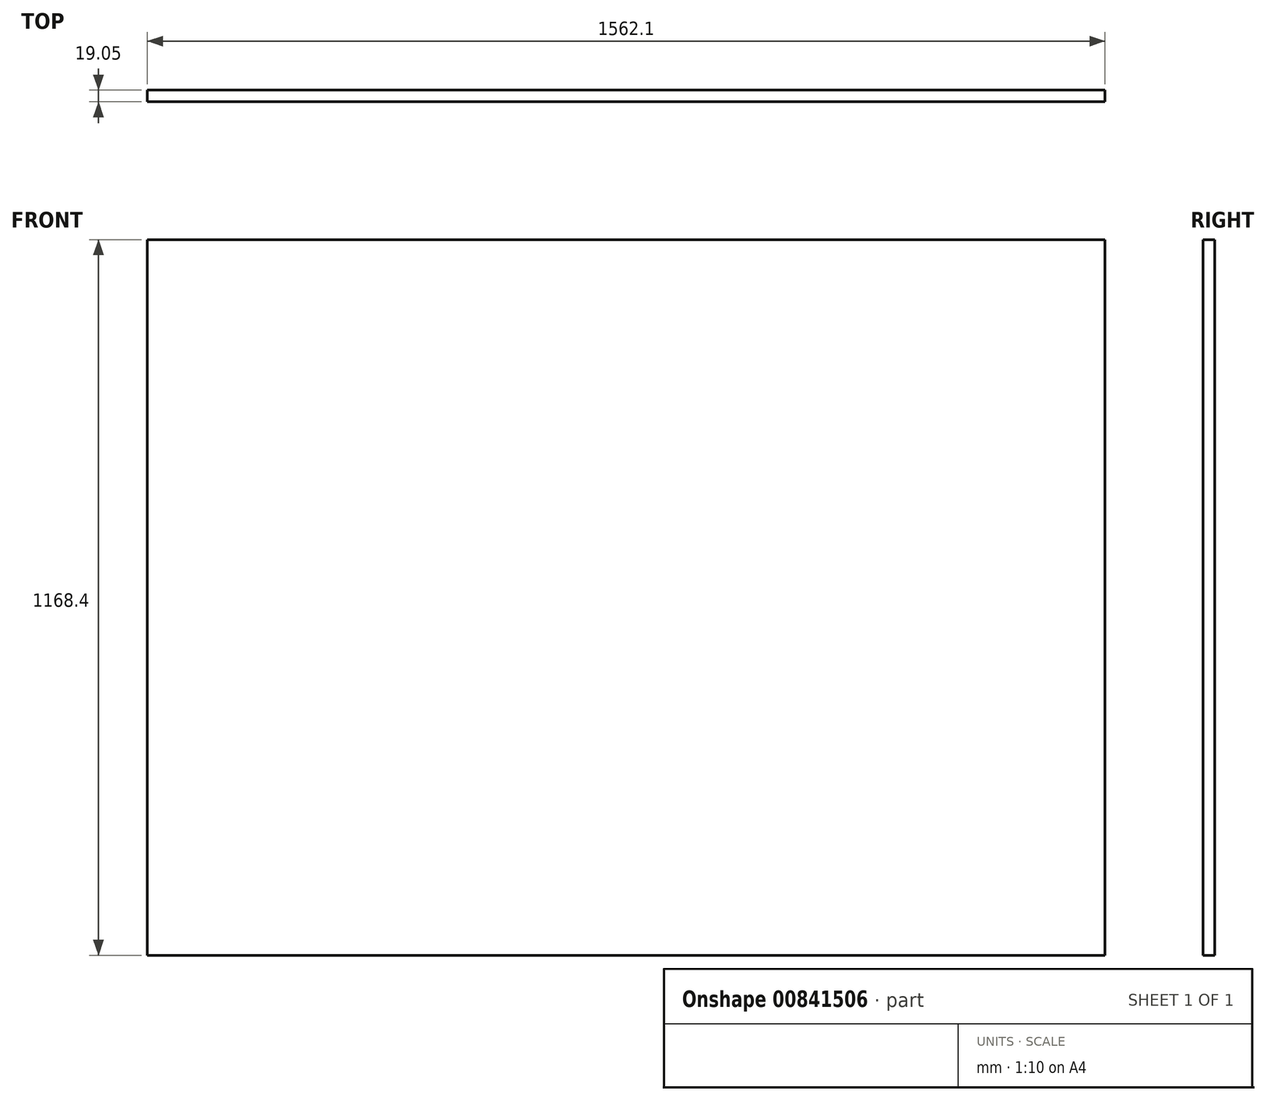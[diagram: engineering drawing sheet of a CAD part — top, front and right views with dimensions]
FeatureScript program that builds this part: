
annotation { "Feature Type Name" : "Feature", "Feature Type Description" : "" }
export const myFeature = defineFeature(function(context is Context, id is Id, definition is map)
    precondition{}
    {
        {
            var Q0;
            Q0=qCreatedBy(makeId("Front.planeOp"),FACE);
            var sketch = newSketch(context, id + "F0", { "sketchPlane" : qUnion([Q0])});
            skLineSegment(sketch, "E0.bottom", {"start": v(0, 0) * mm, "end": v(1562.1, 0) * mm});
            skLineSegment(sketch, "E0.top", {"start": v(0, 1168.4) * mm, "end": v(1562.1, 1168.4) * mm});
            skLineSegment(sketch, "E0.left", {"start": v(0, 0) * mm, "end": v(0, 1168.4) * mm});
            skLineSegment(sketch, "E0.right", {"start": v(1562.1, 0) * mm, "end": v(1562.1, 1168.4) * mm});
            skSolve(sketch);
        }
        {
            var Q0;
            Q0=qSketchRegion(id+"F0",true);
            extrude(context, id + "F1", {"entities" : qUnion([Q0]), "depth" : 19.05 * mm, "offsetDistance" : 25.4 * mm});
        }
    });
